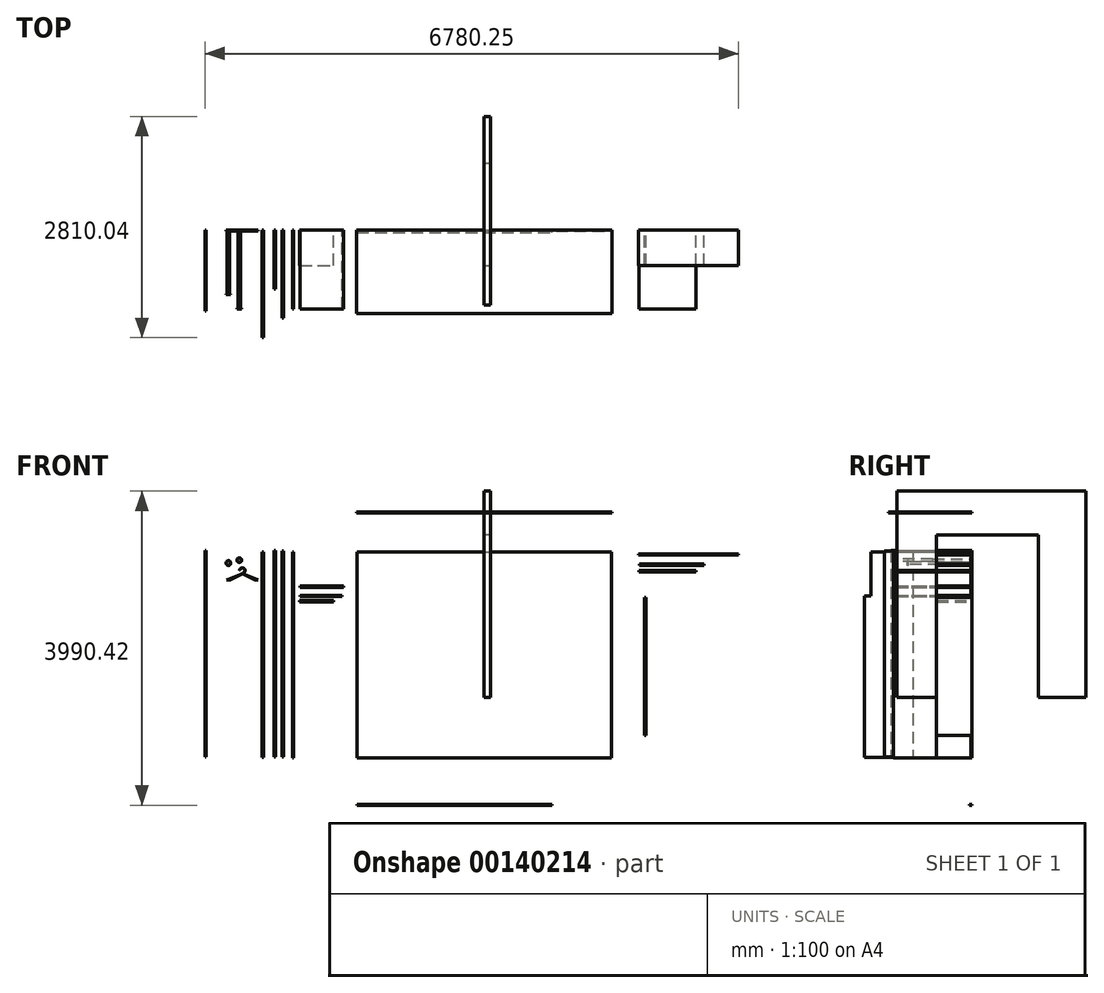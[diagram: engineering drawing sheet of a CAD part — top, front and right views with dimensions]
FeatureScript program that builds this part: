
annotation { "Feature Type Name" : "Feature", "Feature Type Description" : "" }
export const myFeature = defineFeature(function(context is Context, id is Id, definition is map)
    precondition{}
    {
        {
            var Q0;
            Q0=qCreatedBy(makeId("Front.planeOp"),FACE);
            var sketch = newSketch(context, id + "F0", { "sketchPlane" : qUnion([Q0])});
            skLineSegment(sketch, "E0.bottom", {"start": v(-1615, 1310) * mm, "end": v(1615, 1310) * mm});
            skLineSegment(sketch, "E0.top", {"start": v(-1615, -1310) * mm, "end": v(1615, -1310) * mm});
            skLineSegment(sketch, "E0.left", {"start": v(-1615, 1310) * mm, "end": v(-1615, -1310) * mm});
            skLineSegment(sketch, "E0.right", {"start": v(1615, 1310) * mm, "end": v(1615, -1310) * mm});
            skLineSegment(sketch, "E1", {"start": v(0, 1310) * mm, "end": v(0, -1310) * mm, "construction": true});
            skLineSegment(sketch, "E2", {"start": v(-1615, 0) * mm, "end": v(1615, 0) * mm, "construction": true});
            skLineSegment(sketch, "E3", {"start": v(785, 1310) * mm, "end": v(785, -1310) * mm, "construction": true});
            skLineSegment(sketch, "E4", {"start": v(-1065, 1310) * mm, "end": v(-1065, -1310) * mm, "construction": true});
            skLineSegment(sketch, "E5.1.0.0", {"start": v(-515, 1310) * mm, "end": v(-515, -1310) * mm, "construction": true});
            skLineSegment(sketch, "E5.direction1", {"start": v(-1065, -1310) * mm, "end": v(-515, -1310) * mm, "construction": true});
            skLineSegment(sketch, "E6", {"start": v(-1615, -810) * mm, "end": v(-1065, -810) * mm, "construction": true});
            skLineSegment(sketch, "E7", {"start": v(-1615, 860) * mm, "end": v(-1065, 860) * mm, "construction": true});
            skLineSegment(sketch, "E8", {"start": v(-1065, 860) * mm, "end": v(-515, 860) * mm, "construction": true});
            skLineSegment(sketch, "E9", {"start": v(-515, 860) * mm, "end": v(0, 860) * mm, "construction": true});
            skLineSegment(sketch, "E10", {"start": v(0, 860) * mm, "end": v(785, 860) * mm, "construction": true});
            skLineSegment(sketch, "E11", {"start": v(785, 860) * mm, "end": v(1615, 860) * mm, "construction": true});
            skLineSegment(sketch, "E12", {"start": v(-1065, -910) * mm, "end": v(-515, -910) * mm, "construction": true});
            skLineSegment(sketch, "E13", {"start": v(-515, -910) * mm, "end": v(0, -910) * mm, "construction": true});
            skLineSegment(sketch, "E14", {"start": v(0, -910) * mm, "end": v(785, -910) * mm, "construction": true});
            skLineSegment(sketch, "E15", {"start": v(-65, 1310) * mm, "end": v(-65, -1310) * mm, "construction": true});
            skLineSegment(sketch, "E16.bottom", {"start": v(-2436.69, 1310) * mm, "end": v(-2421.69, 1310) * mm});
            skLineSegment(sketch, "E16.top", {"start": v(-2436.69, -1310) * mm, "end": v(-2421.69, -1310) * mm});
            skLineSegment(sketch, "E16.left", {"start": v(-2436.69, 1310) * mm, "end": v(-2436.69, -1310) * mm});
            skLineSegment(sketch, "E16.right", {"start": v(-2421.69, 1310) * mm, "end": v(-2421.69, -1310) * mm});
            skLineSegment(sketch, "E17.bottom", {"start": v(-2340.15, 875) * mm, "end": v(-1790.15, 875) * mm});
            skLineSegment(sketch, "E17.top", {"start": v(-2340.15, 860) * mm, "end": v(-1790.15, 860) * mm});
            skLineSegment(sketch, "E17.left", {"start": v(-2340.15, 875) * mm, "end": v(-2340.15, 860) * mm});
            skLineSegment(sketch, "E17.right", {"start": v(-1790.15, 875) * mm, "end": v(-1790.15, 860) * mm});
            skLineSegment(sketch, "E18.bottom", {"start": v(-2340.15, 754.88) * mm, "end": v(-1805.15, 754.88) * mm});
            skLineSegment(sketch, "E18.top", {"start": v(-2340.15, 739.88) * mm, "end": v(-1805.15, 739.88) * mm});
            skLineSegment(sketch, "E18.left", {"start": v(-2340.15, 754.88) * mm, "end": v(-2340.15, 739.88) * mm});
            skLineSegment(sketch, "E18.right", {"start": v(-1805.15, 754.88) * mm, "end": v(-1805.15, 739.88) * mm});
            skLineSegment(sketch, "E19", {"start": v(865, -1310) * mm, "end": v(865, 1310) * mm, "construction": true});
            skLineSegment(sketch, "E20.bottom", {"start": v(-2567.25, 1321.93) * mm, "end": v(-2552.25, 1321.93) * mm});
            skLineSegment(sketch, "E20.top", {"start": v(-2567.25, -1298.07) * mm, "end": v(-2552.25, -1298.07) * mm});
            skLineSegment(sketch, "E20.left", {"start": v(-2567.25, 1321.93) * mm, "end": v(-2567.25, -1298.07) * mm});
            skLineSegment(sketch, "E20.right", {"start": v(-2552.25, 1321.93) * mm, "end": v(-2552.25, -1298.07) * mm});
            skCircle(sketch, "E21", {"center": v(-3111.6, 1204.6) * mm, "radius": 30 * mm});
            skCircle(sketch, "E22", {"center": v(-3111.6, 1204.6) * mm, "radius": 15 * mm});
            skLineSegment(sketch, "E23", {"start": v(-1615, 710) * mm, "end": v(-1065, 710) * mm, "construction": true});
            skLineSegment(sketch, "E24", {"start": v(-1065, 710) * mm, "end": v(-515, 710) * mm, "construction": true});
            skPoint(sketch, "E25", {"position": v(-1340, 710) * mm});
            skPoint(sketch, "E26", {"position": v(-790, 710) * mm});
            skCircle(sketch, "E27", {"center": v(-3073.55, 1072.23) * mm, "radius": 35 * mm});
            skCircle(sketch, "E28", {"center": v(-3073.55, 1072.23) * mm, "radius": 32.5 * mm});
            skLineSegment(sketch, "E29", {"start": v(-3073.55, 1072.23) * mm, "end": v(-3106.05, 1072.57) * mm});
            skLineSegment(sketch, "E30", {"start": v(-3106.05, 1072.57) * mm, "end": v(-3108.55, 1072.6) * mm});
            skLineSegment(sketch, "E31", {"start": v(-3073.55, 1072.23) * mm, "end": v(-3069.29, 1040) * mm});
            skLineSegment(sketch, "E32", {"start": v(-3069.29, 1040) * mm, "end": v(-3076.37, 1029.3) * mm});
            skLineSegment(sketch, "E33", {"start": v(-3076.37, 1029.3) * mm, "end": v(-3252.83, 959.74) * mm});
            skLineSegment(sketch, "E34", {"start": v(-3062.43, 1029.3) * mm, "end": v(-2887.19, 958.11) * mm});
            skLineSegment(sketch, "E35", {"start": v(-2873.75, 951.6) * mm, "end": v(-2887.19, 958.11) * mm});
            skLineSegment(sketch, "E36", {"start": v(-2873.75, 951.6) * mm, "end": v(-2910.4, 951.6) * mm});
            skLineSegment(sketch, "E37", {"start": v(-2910.4, 951.6) * mm, "end": v(-3063.39, 1026.56) * mm});
            skLineSegment(sketch, "E38", {"start": v(-3063.39, 1026.56) * mm, "end": v(-3074.2, 1026.56) * mm});
            skLineSegment(sketch, "E39", {"start": v(-3074.2, 1026.56) * mm, "end": v(-3231.7, 951.6) * mm});
            skLineSegment(sketch, "E40", {"start": v(-3231.7, 951.6) * mm, "end": v(-3274.82, 951.6) * mm});
            skLineSegment(sketch, "E41", {"start": v(-3274.82, 951.6) * mm, "end": v(-3252.83, 959.74) * mm});
            skLineSegment(sketch, "E42", {"start": v(-3062.43, 1029.3) * mm, "end": v(-3064.58, 1038.4) * mm});
            skLineSegment(sketch, "E43", {"start": v(-3276.36, 912.45) * mm, "end": v(-3076.36, 912.45) * mm, "construction": true});
            skLineSegment(sketch, "E44", {"start": v(-3076.36, 912.45) * mm, "end": v(-2876.36, 912.45) * mm, "construction": true});
            skLineSegment(sketch, "E45.bottom", {"start": v(1961.25, 1284.5) * mm, "end": v(3231.25, 1284.5) * mm});
            skLineSegment(sketch, "E45.top", {"start": v(1961.25, 1269.5) * mm, "end": v(3231.25, 1269.5) * mm});
            skLineSegment(sketch, "E45.left", {"start": v(1961.25, 1284.5) * mm, "end": v(1961.25, 1269.5) * mm});
            skLineSegment(sketch, "E45.right", {"start": v(3231.25, 1284.5) * mm, "end": v(3231.25, 1269.5) * mm});
            skPoint(sketch, "E46.firstSnap0", {"position": v(1200, 860) * mm});
            skLineSegment(sketch, "E47.bottom", {"start": v(2036.18, 730.1) * mm, "end": v(2051.18, 730.1) * mm});
            skLineSegment(sketch, "E47.top", {"start": v(2036.18, -1024.9) * mm, "end": v(2051.18, -1024.9) * mm});
            skLineSegment(sketch, "E47.left", {"start": v(2036.18, 730.1) * mm, "end": v(2036.18, -1024.9) * mm});
            skLineSegment(sketch, "E47.right", {"start": v(2051.18, 730.1) * mm, "end": v(2051.18, -1024.9) * mm});
            skPoint(sketch, "E48", {"position": v(-65, 860) * mm});
            skLineSegment(sketch, "E49.bottom", {"start": v(1969.04, 1153.35) * mm, "end": v(2789.04, 1153.35) * mm});
            skLineSegment(sketch, "E49.top", {"start": v(1969.04, 1138.35) * mm, "end": v(2789.04, 1138.35) * mm});
            skLineSegment(sketch, "E49.left", {"start": v(1969.04, 1153.35) * mm, "end": v(1969.04, 1138.35) * mm});
            skLineSegment(sketch, "E49.right", {"start": v(2789.04, 1153.35) * mm, "end": v(2789.04, 1138.35) * mm});
            skLineSegment(sketch, "E50", {"start": v(-65, 80) * mm, "end": v(785, 80) * mm, "construction": true});
            skCircle(sketch, "E51", {"center": v(-3249.62, 1167.28) * mm, "radius": 30 * mm});
            skCircle(sketch, "E52", {"center": v(-3249.62, 1167.28) * mm, "radius": 15 * mm});
            skLineSegment(sketch, "E53", {"start": v(-65, 470) * mm, "end": v(785, 470) * mm, "construction": true});
            skLineSegment(sketch, "E54.bottom", {"start": v(-2348.88, 690.15) * mm, "end": v(-1913.88, 690.15) * mm});
            skLineSegment(sketch, "E54.top", {"start": v(-2348.88, 675.15) * mm, "end": v(-1913.88, 675.15) * mm});
            skLineSegment(sketch, "E54.left", {"start": v(-2348.88, 690.15) * mm, "end": v(-2348.88, 675.15) * mm});
            skLineSegment(sketch, "E54.right", {"start": v(-1913.88, 690.15) * mm, "end": v(-1913.88, 675.15) * mm});
            skLineSegment(sketch, "E55", {"start": v(-515, -710) * mm, "end": v(-65, -710) * mm, "construction": true});
            skLineSegment(sketch, "E56", {"start": v(-515, -510) * mm, "end": v(-65, -510) * mm, "construction": true});
            skLineSegment(sketch, "E57", {"start": v(-515, -310) * mm, "end": v(-65, -310) * mm, "construction": true});
            skLineSegment(sketch, "E58", {"start": v(-290, -710) * mm, "end": v(-290, -910) * mm, "construction": true});
            skPoint(sketch, "E58.endSnap0", {"position": v(-257.5, -910) * mm});
            skLineSegment(sketch, "E59", {"start": v(-290, -710) * mm, "end": v(-290, -510) * mm, "construction": true});
            skLineSegment(sketch, "E60", {"start": v(-290, -510) * mm, "end": v(-290, -310) * mm, "construction": true});
            skLineSegment(sketch, "E61", {"start": v(-515, 80) * mm, "end": v(-65, 80) * mm, "construction": true});
            skLineSegment(sketch, "E62", {"start": v(-515, 470) * mm, "end": v(-65, 470) * mm, "construction": true});
            skLineSegment(sketch, "E63", {"start": v(-290, -310) * mm, "end": v(-290, 80) * mm, "construction": true});
            skLineSegment(sketch, "E64", {"start": v(-290, 80) * mm, "end": v(-290, 470) * mm, "construction": true});
            skLineSegment(sketch, "E65", {"start": v(-290, 470) * mm, "end": v(-290, 860) * mm, "construction": true});
            skPoint(sketch, "E66", {"position": v(865, 860) * mm});
            skLineSegment(sketch, "E67", {"start": v(865, 470) * mm, "end": v(1615, 470) * mm, "construction": true});
            skLineSegment(sketch, "E68.bottom", {"start": v(1967.3, 1071.9) * mm, "end": v(2687.3, 1071.9) * mm});
            skLineSegment(sketch, "E68.top", {"start": v(1967.3, 1056.9) * mm, "end": v(2687.3, 1056.9) * mm});
            skLineSegment(sketch, "E68.left", {"start": v(1967.3, 1071.9) * mm, "end": v(1967.3, 1056.9) * mm});
            skLineSegment(sketch, "E68.right", {"start": v(2687.3, 1071.9) * mm, "end": v(2687.3, 1056.9) * mm});
            skLineSegment(sketch, "E69.bottom", {"start": v(-2668.04, 1324.6) * mm, "end": v(-2653.04, 1324.6) * mm});
            skLineSegment(sketch, "E69.top", {"start": v(-2668.04, -1295.4) * mm, "end": v(-2653.04, -1295.4) * mm});
            skLineSegment(sketch, "E69.left", {"start": v(-2668.04, 1324.6) * mm, "end": v(-2668.04, -1295.4) * mm});
            skLineSegment(sketch, "E69.right", {"start": v(-2653.04, 1324.6) * mm, "end": v(-2653.04, -1295.4) * mm});
            skLineSegment(sketch, "E70.bottom", {"start": v(-1616.94, -1898.52) * mm, "end": v(863.06, -1898.52) * mm});
            skLineSegment(sketch, "E70.top", {"start": v(-1616.94, -1908.52) * mm, "end": v(863.06, -1908.52) * mm});
            skLineSegment(sketch, "E70.left", {"start": v(-1616.94, -1898.52) * mm, "end": v(-1616.94, -1908.52) * mm});
            skLineSegment(sketch, "E70.right", {"start": v(863.06, -1898.52) * mm, "end": v(863.06, -1908.52) * mm});
            skLineSegment(sketch, "E71.bottom", {"start": v(-2804.48, 1310.2) * mm, "end": v(-2819.48, 1310.2) * mm});
            skLineSegment(sketch, "E71.top", {"start": v(-2804.48, -1299.8) * mm, "end": v(-2819.48, -1299.8) * mm});
            skLineSegment(sketch, "E71.left", {"start": v(-2804.48, 1310.2) * mm, "end": v(-2804.48, -1299.8) * mm});
            skLineSegment(sketch, "E71.right", {"start": v(-2819.48, 1310.2) * mm, "end": v(-2819.48, -1299.8) * mm});
            skLineSegment(sketch, "E72.bottom", {"start": v(-1621.06, 1818.26) * mm, "end": v(1623.94, 1818.26) * mm});
            skLineSegment(sketch, "E72.top", {"start": v(-1621.06, 1803.26) * mm, "end": v(1623.94, 1803.26) * mm});
            skLineSegment(sketch, "E72.left", {"start": v(-1621.06, 1818.26) * mm, "end": v(-1621.06, 1803.26) * mm});
            skLineSegment(sketch, "E72.right", {"start": v(1623.94, 1818.26) * mm, "end": v(1623.94, 1803.26) * mm});
            skLineSegment(sketch, "E73.bottom", {"start": v(-3549, 1324.47) * mm, "end": v(-3534, 1324.47) * mm});
            skLineSegment(sketch, "E73.top", {"start": v(-3549, -1295.53) * mm, "end": v(-3534, -1295.53) * mm});
            skLineSegment(sketch, "E73.left", {"start": v(-3549, 1324.47) * mm, "end": v(-3549, -1295.53) * mm});
            skLineSegment(sketch, "E73.right", {"start": v(-3534, 1324.47) * mm, "end": v(-3534, -1295.53) * mm});
            skSolve(sketch);
        }
        {
            var Q0;
            Q0=makeQuery(id+"F0.imprint","IMPRINT",FACE,{"disambiguationData":[TD([[makeQuery(id+"F0.imprint","IMPRINT",EDGE,{"derivedFrom":sQuery(id+"F0.wireOp",EDGE,"E0.bottom")}),-1.0]])]});
            extrude(context, id + "F1", {"entities" : qUnion([Q0]), "depth" : 15 * mm});
        }
        {
            var Q0;
            Q0=qCreatedBy(makeId("Right.planeOp"),FACE);
            var sketch = newSketch(context, id + "F2", { "sketchPlane" : qUnion([Q0])});
            skLineSegment(sketch, "E74", {"start": v(1445.04, -538.1) * mm, "end": v(1445.04, 2081.9) * mm});
            skLineSegment(sketch, "E75", {"start": v(1445.04, 2081.9) * mm, "end": v(-954.96, 2081.9) * mm});
            skLineSegment(sketch, "E76", {"start": v(-954.96, 2081.9) * mm, "end": v(-954.96, -538.1) * mm});
            skLineSegment(sketch, "E77", {"start": v(-954.96, -538.1) * mm, "end": v(-454.96, -538.1) * mm});
            skLineSegment(sketch, "E78", {"start": v(-454.96, -538.1) * mm, "end": v(-454.96, 1521.9) * mm});
            skLineSegment(sketch, "E79", {"start": v(-454.96, 1521.9) * mm, "end": v(845.04, 1521.9) * mm});
            skLineSegment(sketch, "E80", {"start": v(845.04, 1521.9) * mm, "end": v(845.04, -538.1) * mm});
            skLineSegment(sketch, "E81", {"start": v(845.04, -538.1) * mm, "end": v(1445.04, -538.1) * mm});
            skSolve(sketch);
        }
        {
            var Q0;
            Q0=makeQuery(id+"F2.imprint","IMPRINT",FACE,{"disambiguationData":[TD([[makeQuery(id+"F2.imprint","IMPRINT",EDGE,{"derivedFrom":sQuery(id+"F2.wireOp",EDGE,"E74")}),1.0]])]});
            extrude(context, id + "F3", {"entities" : qUnion([Q0]), "depth" : 80 * mm});
        }
        {
            var Q0;
            Q0=makeQuery(id+"F0.imprint","IMPRINT",FACE,{"disambiguationData":[TD([[makeQuery(id+"F0.imprint","IMPRINT",EDGE,{"derivedFrom":sQuery(id+"F0.wireOp",EDGE,"E16.bottom")}),-1.0]])]});
            extrude(context, id + "F4", {"entities" : qUnion([Q0]), "depth" : 1000 * mm});
        }
        {
            var Q0;
            Q0=makeQuery(id+"F0.imprint","IMPRINT",FACE,{"disambiguationData":[TD([[makeQuery(id+"F0.imprint","IMPRINT",EDGE,{"derivedFrom":sQuery(id+"F0.wireOp",EDGE,"E16.bottom")}),-1.0]])]});
            extrude(context, id + "F5", {"entities" : qUnion([Q0]), "depth" : 450 * mm});
        }
        {
            var Q0;
            Q0=makeQuery(id+"F0.imprint","IMPRINT",FACE,{"disambiguationData":[TD([[makeQuery(id+"F0.imprint","IMPRINT",EDGE,{"derivedFrom":sQuery(id+"F0.wireOp",EDGE,"E17.bottom")}),-1.0]])]});
            extrude(context, id + "F6", {"entities" : qUnion([Q0]), "depth" : 1000 * mm});
        }
        {
            var Q0;
            Q0=makeQuery(id+"F0.imprint","IMPRINT",FACE,{"disambiguationData":[TD([[makeQuery(id+"F0.imprint","IMPRINT",EDGE,{"derivedFrom":sQuery(id+"F0.wireOp",EDGE,"E18.bottom")}),-1.0]])]});
            extrude(context, id + "F7", {"entities" : qUnion([Q0]), "depth" : 1000 * mm});
        }
        {
            var Q0;
            Q0=makeQuery(id+"F0.imprint","IMPRINT",FACE,{"disambiguationData":[TD([[makeQuery(id+"F0.imprint","IMPRINT",EDGE,{"derivedFrom":sQuery(id+"F0.wireOp",EDGE,"E20.bottom")}),-1.0]])]});
            extrude(context, id + "F8", {"entities" : qUnion([Q0]), "depth" : 1115 * mm});
        }
        {
            var Q0;
            Q0=makeQuery(id+"F0.imprint","IMPRINT",FACE,{"disambiguationData":[TD([[makeQuery(id+"F0.imprint","IMPRINT",EDGE,{"derivedFrom":sQuery(id+"F0.wireOp",EDGE,"E21")}),1.0]])]});
            extrude(context, id + "F9", {"entities" : qUnion([Q0]), "depth" : 10 * mm});
        }
        {
            var Q0;
            Q0=makeQuery(id+"F0.imprint","IMPRINT",FACE,{"disambiguationData":[TD([[makeQuery(id+"F0.imprint","IMPRINT",EDGE,{"derivedFrom":sQuery(id+"F0.wireOp",EDGE,"E22")}),1.0]])]});
            extrude(context, id + "F10", {"entities" : qUnion([Q0]), "operationType" : NewBodyOperationType.ADD, "depth" : 500 * mm});
        }
        {
            var Q0;
            Q0=makeQuery(id+"F9.opExtrude","SWEPT_BODY",BODY,{"disambiguationData":[OSD([sQuery(id+"F0.wireOp",EDGE,"E21"),sQuery(id+"F0.wireOp",EDGE,"E22")])]});
            var Q1;
            Q1=makeQuery(id+"F10.opExtrude","CAP_FACE",FACE,{"disambiguationData":[OSD([sQuery(id+"F0.wireOp",EDGE,"E22")])],"isStart":false});
            mirror(context, id + "F11", {"operationType" : NewBodyOperationType.ADD, "entities" : qUnion([Q0]), "mirrorPlane" : qUnion([Q1])});
        }
        {
            var Q0;
            {var subQ0=sQuery(id+"F0.wireOp",EDGE,"E30");Q0=makeQuery(id+"F0.imprint","IMPRINT",FACE,{"disambiguationData":[TD([[makeQuery(id+"F0.imprint","IMPRINT",EDGE,{"derivedFrom":subQ0}),-1.0]])]});}
            var Q1;
            {var subQ1=sQuery(id+"F0.wireOp",EDGE,"E33");Q1=makeQuery(id+"F0.imprint","IMPRINT",FACE,{"disambiguationData":[TD([[makeQuery(id+"F0.imprint","IMPRINT",EDGE,{"derivedFrom":subQ1}),1.0]])]});}
            extrude(context, id + "F12", {"entities" : qUnion([Q0, Q1]), "depth" : 10 * mm});
        }
        {
            var Q0;
            Q0=makeQuery(id+"F0.imprint","IMPRINT",FACE,{"disambiguationData":[TD([[makeQuery(id+"F0.imprint","IMPRINT",EDGE,{"derivedFrom":sQuery(id+"F0.wireOp",EDGE,"E45.bottom")}),-1.0]])]});
            extrude(context, id + "F13", {"entities" : qUnion([Q0]), "depth" : 450 * mm});
        }
        {
            var Q0;
            Q0=makeQuery(id+"F0.imprint","IMPRINT",FACE,{"disambiguationData":[TD([[makeQuery(id+"F0.imprint","IMPRINT",EDGE,{"derivedFrom":sQuery(id+"F0.wireOp",EDGE,"E47.bottom")}),-1.0]])]});
            extrude(context, id + "F14", {"entities" : qUnion([Q0]), "depth" : 450 * mm});
        }
        {
            var Q0;
            Q0=makeQuery(id+"F0.imprint","IMPRINT",FACE,{"disambiguationData":[TD([[makeQuery(id+"F0.imprint","IMPRINT",EDGE,{"derivedFrom":sQuery(id+"F0.wireOp",EDGE,"E49.bottom")}),-1.0]])]});
            extrude(context, id + "F15", {"entities" : qUnion([Q0]), "depth" : 450 * mm});
        }
        {
            var Q0;
            Q0=makeQuery(id+"F0.imprint","IMPRINT",FACE,{"disambiguationData":[TD([[makeQuery(id+"F0.imprint","IMPRINT",EDGE,{"derivedFrom":sQuery(id+"F0.wireOp",EDGE,"E51")}),1.0]])]});
            extrude(context, id + "F16", {"entities" : qUnion([Q0]), "depth" : 10 * mm});
        }
        {
            var Q0;
            Q0=makeQuery(id+"F0.imprint","IMPRINT",FACE,{"disambiguationData":[TD([[makeQuery(id+"F0.imprint","IMPRINT",EDGE,{"derivedFrom":sQuery(id+"F0.wireOp",EDGE,"E52")}),1.0]])]});
            extrude(context, id + "F17", {"entities" : qUnion([Q0]), "operationType" : NewBodyOperationType.ADD, "depth" : 410 * mm});
        }
        {
            var Q0;
            Q0=makeQuery(id+"F16.opExtrude","SWEPT_BODY",BODY,{"disambiguationData":[OSD([sQuery(id+"F0.wireOp",EDGE,"E51"),sQuery(id+"F0.wireOp",EDGE,"E52")])]});
            var Q1;
            Q1=makeQuery(id+"F17.opExtrude","CAP_FACE",FACE,{"disambiguationData":[OSD([sQuery(id+"F0.wireOp",EDGE,"E52")])],"isStart":false});
            mirror(context, id + "F18", {"operationType" : NewBodyOperationType.ADD, "entities" : qUnion([Q0]), "mirrorPlane" : qUnion([Q1])});
        }
        {
            var Q0;
            Q0=makeQuery(id+"F0.imprint","IMPRINT",FACE,{"disambiguationData":[TD([[makeQuery(id+"F0.imprint","IMPRINT",EDGE,{"derivedFrom":sQuery(id+"F0.wireOp",EDGE,"E54.bottom")}),-1.0]])]});
            extrude(context, id + "F19", {"entities" : qUnion([Q0]), "depth" : 450 * mm});
        }
        {
            var Q0;
            Q0=makeQuery(id+"F0.imprint","IMPRINT",FACE,{"disambiguationData":[TD([[makeQuery(id+"F0.imprint","IMPRINT",EDGE,{"derivedFrom":sQuery(id+"F0.wireOp",EDGE,"E68.bottom")}),-1.0]])]});
            extrude(context, id + "F20", {"entities" : qUnion([Q0]), "depth" : 1000 * mm});
        }
        {
            var Q0;
            Q0=makeQuery(id+"F0.imprint","IMPRINT",FACE,{"disambiguationData":[TD([[makeQuery(id+"F0.imprint","IMPRINT",EDGE,{"derivedFrom":sQuery(id+"F0.wireOp",EDGE,"E69.bottom")}),-1.0]])]});
            extrude(context, id + "F21", {"entities" : qUnion([Q0]), "depth" : 750 * mm});
        }
        {
            var Q0;
            Q0=makeQuery(id+"F0.imprint","IMPRINT",FACE,{"disambiguationData":[TD([[makeQuery(id+"F0.imprint","IMPRINT",EDGE,{"derivedFrom":sQuery(id+"F0.wireOp",EDGE,"E70.bottom")}),-1.0]])]});
            extrude(context, id + "F22", {"entities" : qUnion([Q0]), "depth" : 30 * mm});
        }
        {
            var Q0;
            Q0=makeQuery(id+"F0.imprint","IMPRINT",FACE,{"disambiguationData":[TD([[makeQuery(id+"F0.imprint","IMPRINT",EDGE,{"derivedFrom":sQuery(id+"F0.wireOp",EDGE,"E71.bottom")}),1.0]])]});
            extrude(context, id + "F23", {"entities" : qUnion([Q0]), "depth" : 1365 * mm});
        }
        {
            var Q0;
            Q0=makeQuery(id+"F23.opExtrude","SWEPT_FACE",FACE,{"disambiguationData":[OSD([sQuery(id+"F0.wireOp",EDGE,"E71.right")])]});
            var sketch = newSketch(context, id + "F24", { "sketchPlane" : qUnion([Q0])});
            skLineSegment(sketch, "E82", {"start": v(1285, 1310.2) * mm, "end": v(1285, 750.2) * mm});
            skLineSegment(sketch, "E83", {"start": v(1285, 750.2) * mm, "end": v(1365, 750.2) * mm});
            skSolve(sketch);
        }
        {
            var Q0;
            Q0=qSketchRegion(id+"F24",true);
            var Q1;
            {var subQ0=sQuery(id+"F24.wireOp",EDGE,"E82");Q1=makeQuery(id+"F24.imprint","IMPRINT",FACE,{"disambiguationData":[TD([[makeQuery(id+"F24.imprint","IMPRINT",EDGE,{"derivedFrom":subQ0}),1.0]])]});}
            extrude(context, id + "F25", {"entities" : qUnion([Q0, Q1]), "operationType" : NewBodyOperationType.REMOVE, "oppositeDirection" : true, "depth" : 25 * mm});
        }
        {
            var Q0;
            Q0=makeQuery(id+"F0.imprint","IMPRINT",FACE,{"disambiguationData":[TD([[makeQuery(id+"F0.imprint","IMPRINT",EDGE,{"derivedFrom":sQuery(id+"F0.wireOp",EDGE,"E72.bottom")}),-1.0]])]});
            extrude(context, id + "F26", {"entities" : qUnion([Q0]), "depth" : 1060 * mm});
        }
        {
            var Q0;
            Q0=makeQuery(id+"F0.imprint","IMPRINT",FACE,{"disambiguationData":[TD([[makeQuery(id+"F0.imprint","IMPRINT",EDGE,{"derivedFrom":sQuery(id+"F0.wireOp",EDGE,"E73.bottom")}),-1.0]])]});
            extrude(context, id + "F27", {"entities" : qUnion([Q0]), "depth" : 1030 * mm});
        }
    });
